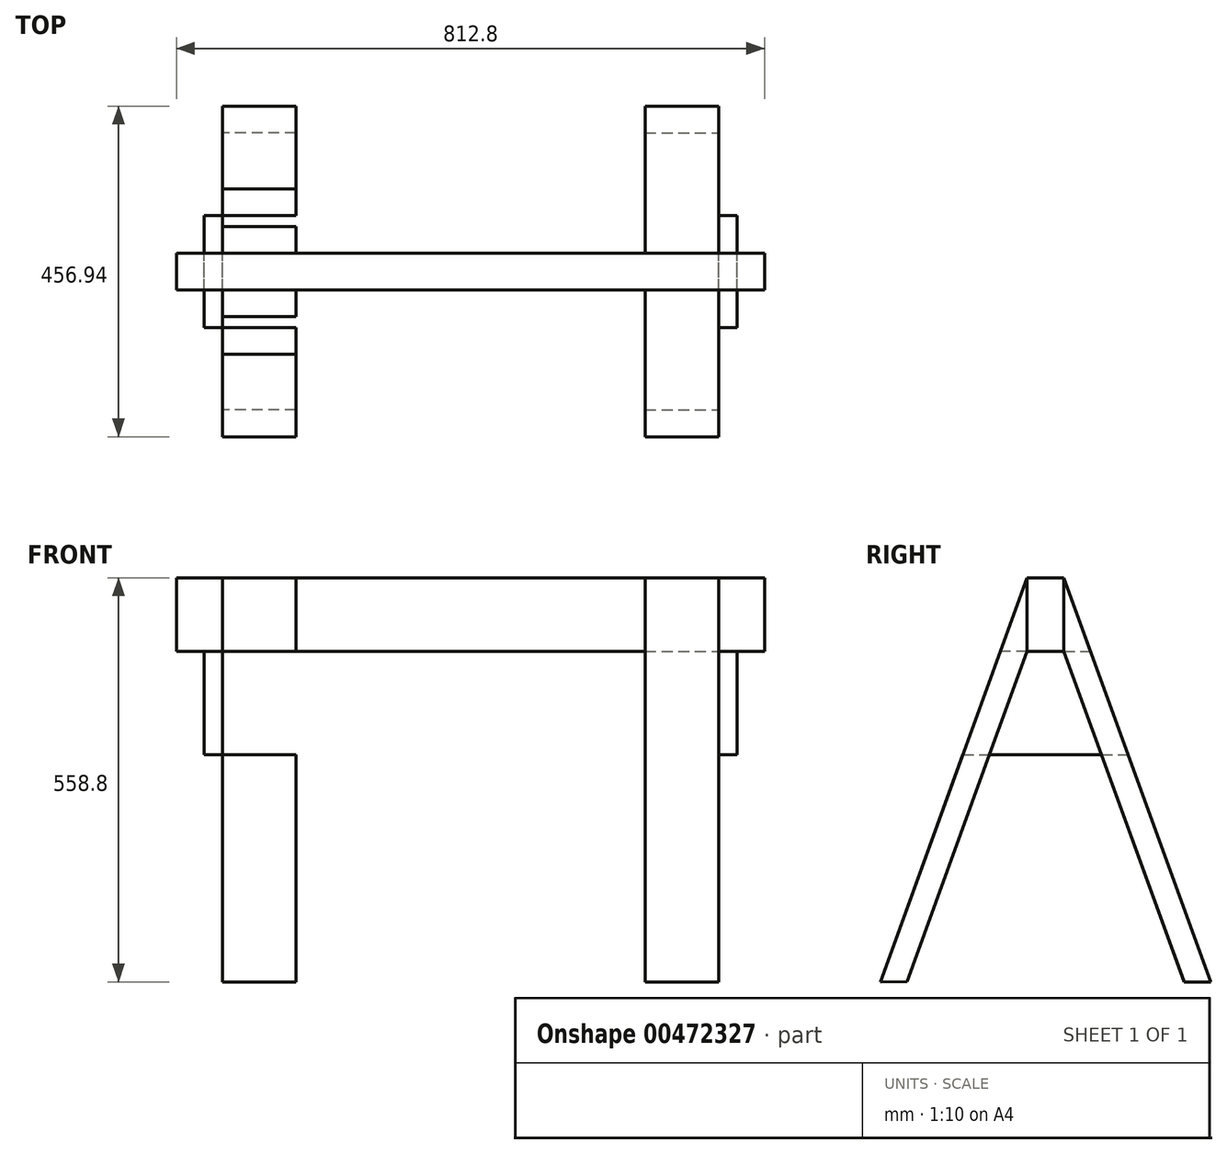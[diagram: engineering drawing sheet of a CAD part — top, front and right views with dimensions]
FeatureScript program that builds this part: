
annotation { "Feature Type Name" : "Feature", "Feature Type Description" : "" }
export const myFeature = defineFeature(function(context is Context, id is Id, definition is map)
    precondition{}
    {
        {
            var Q0;
            Q0=qCreatedBy(makeId("Right.planeOp"),FACE);
            var sketch = newSketch(context, id + "F0", { "sketchPlane" : qUnion([Q0])});
            skLineSegment(sketch, "E0.bottom", {"start": v(-17.01, 50.62) * mm, "end": v(33.79, 50.62) * mm});
            skLineSegment(sketch, "E0.top", {"start": v(-17.01, -50.98) * mm, "end": v(33.79, -50.98) * mm});
            skLineSegment(sketch, "E0.left", {"start": v(-17.01, 50.62) * mm, "end": v(-17.01, -50.98) * mm});
            skLineSegment(sketch, "E0.right", {"start": v(33.79, 50.62) * mm, "end": v(33.79, -50.98) * mm});
            skPoint(sketch, "E1.endSnap0", {"position": v(8.39, -50.98) * mm});
            skLineSegment(sketch, "E2", {"start": v(-219.95, -508.18) * mm, "end": v(-17.01, 50.62) * mm});
            skLineSegment(sketch, "E3", {"start": v(-182.99, -508.02) * mm, "end": v(-17.01, -50.98) * mm});
            skLineSegment(sketch, "E4", {"start": v(236.99, -508.18) * mm, "end": v(33.79, 50.62) * mm});
            skLineSegment(sketch, "E5", {"start": v(33.79, -50.98) * mm, "end": v(199.98, -508.02) * mm});
            skLineSegment(sketch, "E6", {"start": v(-219.95, -508.18) * mm, "end": v(-182.99, -508.02) * mm});
            skLineSegment(sketch, "E7", {"start": v(199.98, -508.02) * mm, "end": v(236.99, -508.18) * mm});
            skLineSegment(sketch, "E8", {"start": v(-53.91, -50.98) * mm, "end": v(70.73, -50.98) * mm});
            skLineSegment(sketch, "E9", {"start": v(-53.91, -50.98) * mm, "end": v(-105.93, -194.23) * mm});
            skLineSegment(sketch, "E10", {"start": v(70.73, -50.98) * mm, "end": v(122.81, -194.2) * mm});
            skLineSegment(sketch, "E11", {"start": v(-105.93, -194.23) * mm, "end": v(122.81, -194.2) * mm});
            skSolve(sketch);
        }
        {
            var Q0;
            Q0=makeQuery(id+"F0.imprint","IMPRINT",FACE,{"disambiguationData":[TD([[makeQuery(id+"F0.imprint","IMPRINT",EDGE,{"derivedFrom":sQuery(id+"F0.wireOp",EDGE,"E0.bottom")}),-1.0]])]});
            extrude(context, id + "F1", {"entities" : qUnion([Q0]), "depth" : 63.5 * mm});
        }
        {
            var Q0;
            {var subQ0=sQuery(id+"F0.wireOp",EDGE,"E0.right");Q0=makeQuery(id+"F0.imprint","IMPRINT",FACE,{"disambiguationData":[TD([[makeQuery(id+"F0.imprint","IMPRINT",EDGE,{"derivedFrom":subQ0}),1.0]])]});}
            var Q1;
            {var subQ0=sQuery(id+"F0.wireOp",EDGE,"E6");Q1=makeQuery(id+"F0.imprint","IMPRINT",FACE,{"disambiguationData":[TD([[makeQuery(id+"F0.imprint","IMPRINT",EDGE,{"derivedFrom":subQ0}),1.0]])]});}
            var Q2;
            {var subQ0=sQuery(id+"F0.wireOp",EDGE,"E7");Q2=makeQuery(id+"F0.imprint","IMPRINT",FACE,{"disambiguationData":[TD([[makeQuery(id+"F0.imprint","IMPRINT",EDGE,{"derivedFrom":subQ0}),1.0]])]});}
            var Q3;
            {var subQ0=sQuery(id+"F0.wireOp",EDGE,"E8");var subQ1=sQuery(id+"F0.wireOp",EDGE,"E4");var subQ2=makeQuery(id+"F0.imprint","INTERSECT",VERTEX,{"derivedFrom":[subQ1,subQ0]});Q3=makeQuery(id+"F0.imprint","IMPRINT",FACE,{"disambiguationData":[TD([[makeQuery(id+"F0.imprint","IMPRINT",EDGE,{"disambiguationData":[TD([[subQ2,1.0]])],"derivedFrom":subQ1}),1.0]])]});}
            var Q4;
            {var subQ0=sQuery(id+"F0.wireOp",EDGE,"E8");var subQ1=sQuery(id+"F0.wireOp",EDGE,"E2");var subQ2=makeQuery(id+"F0.imprint","INTERSECT",VERTEX,{"derivedFrom":[subQ1,subQ0]});Q4=makeQuery(id+"F0.imprint","IMPRINT",FACE,{"disambiguationData":[TD([[makeQuery(id+"F0.imprint","IMPRINT",EDGE,{"disambiguationData":[TD([[subQ2,1.0]])],"derivedFrom":subQ1}),-1.0]])]});}
            var Q5;
            {var subQ0=sQuery(id+"F0.wireOp",EDGE,"E0.left");Q5=makeQuery(id+"F0.imprint","IMPRINT",FACE,{"disambiguationData":[TD([[makeQuery(id+"F0.imprint","IMPRINT",EDGE,{"derivedFrom":subQ0}),-1.0]])]});}
            var Q6;
            {var subQ5=sQuery(id+"F0.wireOp",EDGE,"E9");Q6=makeQuery(id+"F0.imprint","IMPRINT",FACE,{"disambiguationData":[TD([[makeQuery(id+"F0.imprint","IMPRINT",EDGE,{"derivedFrom":subQ5}),1.0]])]});}
            var Q7;
            {var subQ5=sQuery(id+"F0.wireOp",EDGE,"E10");Q7=makeQuery(id+"F0.imprint","IMPRINT",FACE,{"disambiguationData":[TD([[makeQuery(id+"F0.imprint","IMPRINT",EDGE,{"derivedFrom":subQ5}),-1.0]])]});}
            extrude(context, id + "F2", {"entities" : qUnion([Q0, Q1, Q2, Q3, Q4, Q5, Q6, Q7]), "oppositeDirection" : true, "depth" : 101.6 * mm});
        }
        {
            var Q0;
            Q0=makeQuery(id+"F0.imprint","IMPRINT",FACE,{"disambiguationData":[TD([[makeQuery(id+"F0.imprint","IMPRINT",EDGE,{"derivedFrom":sQuery(id+"F0.wireOp",EDGE,"E0.bottom")}),-1.0]])]});
            extrude(context, id + "F3", {"entities" : qUnion([Q0]), "operationType" : NewBodyOperationType.ADD, "oppositeDirection" : true, "depth" : 685.8 * mm});
        }
        {
            var Q0;
            {var subQ1=sQuery(id+"F0.wireOp",EDGE,"E3");var subQ3=sQuery(id+"F0.wireOp",EDGE,"E11");var subQ4=makeQuery(id+"F0.imprint","INTERSECT",VERTEX,{"derivedFrom":[subQ1,subQ3]});Q0=makeQuery(id+"F0.imprint","IMPRINT",FACE,{"disambiguationData":[TD([[makeQuery(id+"F0.imprint","IMPRINT",EDGE,{"disambiguationData":[TD([[subQ4,-1.0]])],"derivedFrom":subQ3}),1.0]])]});}
            var Q1;
            {var subQ5=sQuery(id+"F0.wireOp",EDGE,"E9");Q1=makeQuery(id+"F0.imprint","IMPRINT",FACE,{"disambiguationData":[TD([[makeQuery(id+"F0.imprint","IMPRINT",EDGE,{"derivedFrom":subQ5}),1.0]])]});}
            var Q2;
            {var subQ5=sQuery(id+"F0.wireOp",EDGE,"E10");Q2=makeQuery(id+"F0.imprint","IMPRINT",FACE,{"disambiguationData":[TD([[makeQuery(id+"F0.imprint","IMPRINT",EDGE,{"derivedFrom":subQ5}),-1.0]])]});}
            extrude(context, id + "F4", {"entities" : qUnion([Q0, Q1, Q2]), "depth" : 25.4 * mm});
        }
        {
            var Q0;
            Q0=makeQuery(id+"F3.opExtrude","CAP_FACE",FACE,{"disambiguationData":[OSD([sQuery(id+"F0.wireOp",EDGE,"E0.bottom"),sQuery(id+"F0.wireOp",EDGE,"E0.left"),sQuery(id+"F0.wireOp",EDGE,"E0.right"),sQuery(id+"F0.wireOp",EDGE,"E8")])],"isStart":false});
            var sketch = newSketch(context, id + "F5", { "sketchPlane" : qUnion([Q0])});
            skLineSegment(sketch, "E12", {"start": v(-8.39, 50.62) * mm, "end": v(-18.42, -508.1) * mm});
            skLineSegment(sketch, "E13", {"start": v(-33.79, 50.62) * mm, "end": v(-236.99, -508.18) * mm});
            skLineSegment(sketch, "E14", {"start": v(-236.99, -508.18) * mm, "end": v(-199.95, -508.18) * mm});
            skLineSegment(sketch, "E15", {"start": v(-199.95, -508.18) * mm, "end": v(-33.79, -50.98) * mm});
            skLineSegment(sketch, "E16", {"start": v(-33.79, -50.98) * mm, "end": v(-33.79, 50.62) * mm});
            skLineSegment(sketch, "E17", {"start": v(-33.79, -50.98) * mm, "end": v(-70.73, -50.98) * mm});
            skLineSegment(sketch, "E18", {"start": v(-70.73, -50.98) * mm, "end": v(17.01, -50.98) * mm});
            skLineSegment(sketch, "E19", {"start": v(17.01, 50.62) * mm, "end": v(219.95, -508.18) * mm});
            skLineSegment(sketch, "E20", {"start": v(219.95, -508.18) * mm, "end": v(182.9, -507.52) * mm});
            skLineSegment(sketch, "E21", {"start": v(182.9, -507.52) * mm, "end": v(17.01, -50.98) * mm});
            skLineSegment(sketch, "E22", {"start": v(17.01, 50.62) * mm, "end": v(17.01, -50.98) * mm});
            skLineSegment(sketch, "E23", {"start": v(-70.73, -50.98) * mm, "end": v(53.91, -50.98) * mm});
            skLineSegment(sketch, "E24", {"start": v(53.91, -50.98) * mm, "end": v(105.93, -194.23) * mm});
            skLineSegment(sketch, "E25", {"start": v(-70.73, -50.98) * mm, "end": v(-122.92, -194.5) * mm});
            skLineSegment(sketch, "E26", {"start": v(105.93, -194.23) * mm, "end": v(-122.82, -194.23) * mm});
            skLineSegment(sketch, "E27", {"start": v(-70.73, -50.98) * mm, "end": v(-122.82, -194.23) * mm});
            skSolve(sketch);
        }
        {
            var Q0;
            {var subQ0=sQuery(id+"F5.wireOp",EDGE,"E22");Q0=makeQuery(id+"F5.imprint","IMPRINT",FACE,{"disambiguationData":[TD([[makeQuery(id+"F5.imprint","IMPRINT",EDGE,{"derivedFrom":subQ0}),1.0]])]});}
            var Q1;
            {var subQ0=sQuery(id+"F5.wireOp",EDGE,"E16");Q1=makeQuery(id+"F5.imprint","IMPRINT",FACE,{"disambiguationData":[TD([[makeQuery(id+"F5.imprint","IMPRINT",EDGE,{"derivedFrom":subQ0}),-1.0]])]});}
            var Q2;
            {var subQ5=sQuery(id+"F5.wireOp",EDGE,"E27");Q2=makeQuery(id+"F5.imprint","IMPRINT",FACE,{"disambiguationData":[TD([[makeQuery(id+"F5.imprint","IMPRINT",EDGE,{"derivedFrom":subQ5}),1.0]])]});}
            var Q3;
            {var subQ1=sQuery(id+"F5.wireOp",EDGE,"E14");Q3=makeQuery(id+"F5.imprint","IMPRINT",FACE,{"disambiguationData":[TD([[makeQuery(id+"F5.imprint","IMPRINT",EDGE,{"derivedFrom":subQ1}),1.0]])]});}
            var Q4;
            {var subQ5=sQuery(id+"F5.wireOp",EDGE,"E24");Q4=makeQuery(id+"F5.imprint","IMPRINT",FACE,{"disambiguationData":[TD([[makeQuery(id+"F5.imprint","IMPRINT",EDGE,{"derivedFrom":subQ5}),-1.0]])]});}
            var Q5;
            {var subQ0=sQuery(id+"F5.wireOp",EDGE,"E20");Q5=makeQuery(id+"F5.imprint","IMPRINT",FACE,{"disambiguationData":[TD([[makeQuery(id+"F5.imprint","IMPRINT",EDGE,{"derivedFrom":subQ0}),-1.0]])]});}
            extrude(context, id + "F6", {"entities" : qUnion([Q0, Q1, Q2, Q3, Q4, Q5]), "oppositeDirection" : true, "depth" : 101.6 * mm});
        }
        {
            var Q0;
            Q0=makeQuery(id+"F3.opExtrude","CAP_FACE",FACE,{"disambiguationData":[OSD([sQuery(id+"F0.wireOp",EDGE,"E0.bottom"),sQuery(id+"F0.wireOp",EDGE,"E0.left"),sQuery(id+"F0.wireOp",EDGE,"E0.right"),sQuery(id+"F0.wireOp",EDGE,"E8")])],"isStart":false});
            extrude(context, id + "F7", {"entities" : qUnion([Q0]), "operationType" : NewBodyOperationType.ADD, "depth" : 63.5 * mm});
        }
        {
            var Q0;
            {var subQ0=sQuery(id+"F5.wireOp",EDGE,"E26");var subQ1=sQuery(id+"F5.wireOp",EDGE,"E12");var subQ2=makeQuery(id+"F5.imprint","INTERSECT",VERTEX,{"derivedFrom":[subQ1,subQ0]});Q0=makeQuery(id+"F5.imprint","IMPRINT",FACE,{"disambiguationData":[TD([[makeQuery(id+"F5.imprint","IMPRINT",EDGE,{"disambiguationData":[TD([[subQ2,1.0]])],"derivedFrom":subQ1}),-1.0]])]});}
            var Q1;
            {var subQ5=sQuery(id+"F5.wireOp",EDGE,"E27");Q1=makeQuery(id+"F5.imprint","IMPRINT",FACE,{"disambiguationData":[TD([[makeQuery(id+"F5.imprint","IMPRINT",EDGE,{"derivedFrom":subQ5}),1.0]])]});}
            var Q2;
            {var subQ0=sQuery(id+"F5.wireOp",EDGE,"E26");var subQ1=sQuery(id+"F5.wireOp",EDGE,"E12");var subQ2=makeQuery(id+"F5.imprint","INTERSECT",VERTEX,{"derivedFrom":[subQ1,subQ0]});Q2=makeQuery(id+"F5.imprint","IMPRINT",FACE,{"disambiguationData":[TD([[makeQuery(id+"F5.imprint","IMPRINT",EDGE,{"disambiguationData":[TD([[subQ2,1.0]])],"derivedFrom":subQ1}),1.0]])]});}
            var Q3;
            {var subQ5=sQuery(id+"F5.wireOp",EDGE,"E24");Q3=makeQuery(id+"F5.imprint","IMPRINT",FACE,{"disambiguationData":[TD([[makeQuery(id+"F5.imprint","IMPRINT",EDGE,{"derivedFrom":subQ5}),-1.0]])]});}
            extrude(context, id + "F8", {"entities" : qUnion([Q0, Q1, Q2, Q3]), "depth" : 25.4 * mm});
        }
    });
